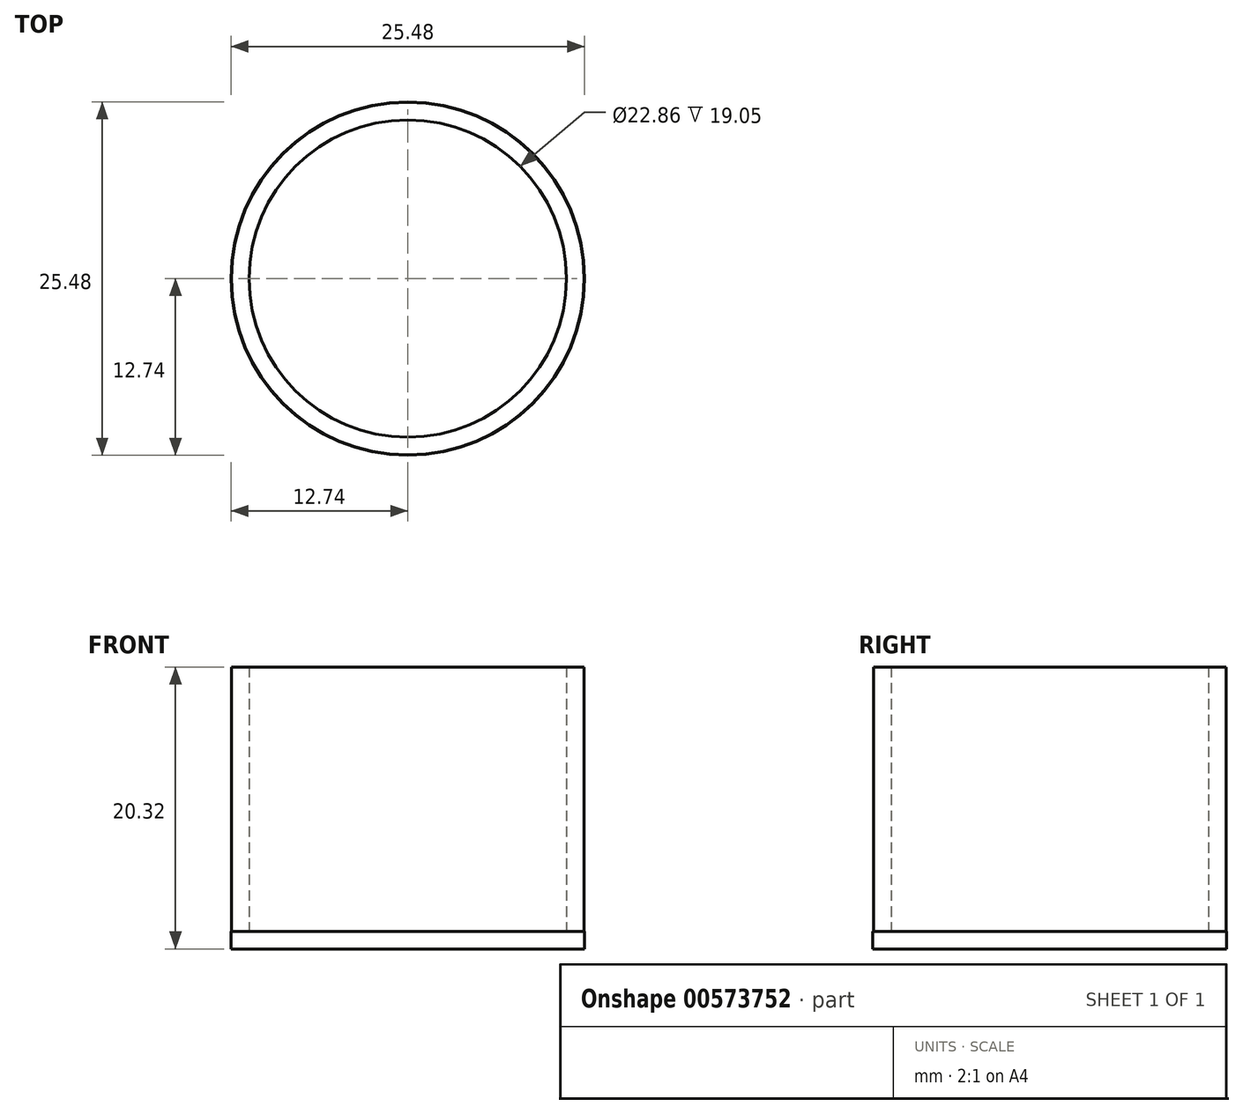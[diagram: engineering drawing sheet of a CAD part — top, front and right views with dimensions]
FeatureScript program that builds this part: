
annotation { "Feature Type Name" : "Feature", "Feature Type Description" : "" }
export const myFeature = defineFeature(function(context is Context, id is Id, definition is map)
    precondition{}
    {
        {
            var Q0;
            Q0=qCreatedBy(makeId("Top.planeOp"),FACE);
            var sketch = newSketch(context, id + "F0", { "sketchPlane" : qUnion([Q0])});
            skCircle(sketch, "E0", {"center": v(0, 0) * mm, "radius": 12.7 * mm});
            skCircle(sketch, "E1", {"center": v(0, 0) * mm, "radius": 11.43 * mm});
            skSolve(sketch);
        }
        {
            var Q0;
            Q0 = qSketchRegion(id + "F0", true);
            extrude(context, id + "F1", {"entities" : qUnion([Q0]), "depth" : 19.05 * mm, "offsetDistance" : 25.4 * mm});
        }
        {
            var Q0;
            Q0=makeQuery(id+"F1.opExtrude","CAP_FACE",FACE,{"disambiguationData":[OSD([sQuery(id+"F0.wireOp",EDGE,"E0"),sQuery(id+"F0.wireOp",EDGE,"E1")])],"isStart":true});
            var sketch = newSketch(context, id + "F2", { "sketchPlane" : qUnion([Q0])});
            skCircle(sketch, "E2", {"center": v(0, 0) * mm, "radius": 12.74 * mm});
            skSolve(sketch);
        }
        {
            var Q0;
            Q0 = qSketchRegion(id + "F2", true);
            extrude(context, id + "F3", {"entities" : qUnion([Q0]), "operationType" : NewBodyOperationType.ADD, "depth" : 1.27 * mm, "offsetDistance" : 25.4 * mm});
        }
    });
